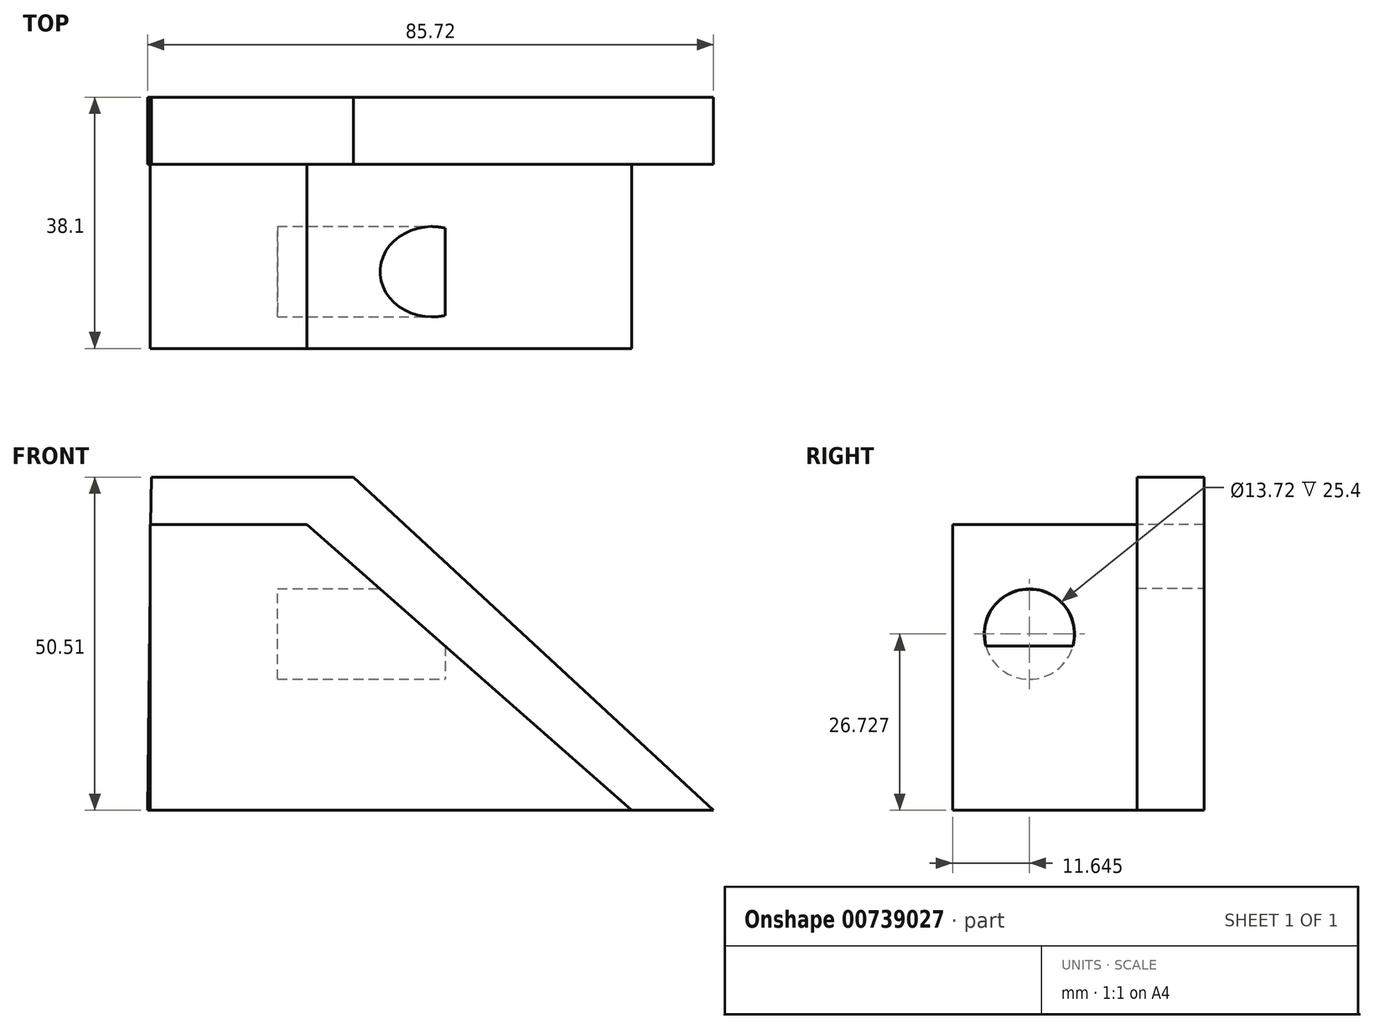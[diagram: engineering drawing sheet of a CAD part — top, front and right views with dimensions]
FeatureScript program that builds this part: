
annotation { "Feature Type Name" : "Feature", "Feature Type Description" : "" }
export const myFeature = defineFeature(function(context is Context, id is Id, definition is map)
    precondition{}
    {
        {
            var Q0;
            Q0=qCreatedBy(makeId("Front.planeOp"),FACE);
            var sketch = newSketch(context, id + "F0", { "sketchPlane" : qUnion([Q0])});
            skLineSegment(sketch, "E0", {"start": v(-44.52, 33.83) * mm, "end": v(-13.92, 33.83) * mm});
            skLineSegment(sketch, "E1", {"start": v(-13.92, 33.83) * mm, "end": v(40.65, -16.68) * mm});
            skLineSegment(sketch, "E2", {"start": v(40.65, -16.68) * mm, "end": v(-45.07, -16.68) * mm});
            skLineSegment(sketch, "E3", {"start": v(-45.07, -16.68) * mm, "end": v(-44.52, 33.83) * mm});
            skSolve(sketch);
        }
        {
            var Q0;
            Q0 = qSketchRegion(id + "F0", true);
            extrude(context, id + "F1", {"entities" : qUnion([Q0]), "depth" : 10.16 * mm, "offsetDistance" : 25.4 * mm});
        }
        {
            var Q0;
            Q0=qCreatedBy(makeId("Front.planeOp"),FACE);
            var sketch = newSketch(context, id + "F2", { "sketchPlane" : qUnion([Q0])});
            skLineSegment(sketch, "E4", {"start": v(-44.7, 28.85) * mm, "end": v(-44.7, -16.68) * mm});
            skLineSegment(sketch, "E5", {"start": v(-44.7, -16.68) * mm, "end": v(28.3, -16.68) * mm});
            skLineSegment(sketch, "E6", {"start": v(28.3, -16.68) * mm, "end": v(-20.92, 26.64) * mm});
            skLineSegment(sketch, "E7", {"start": v(-20.92, 26.64) * mm, "end": v(-44.7, 26.64) * mm});
            skLineSegment(sketch, "E8", {"start": v(-44.7, 26.64) * mm, "end": v(-44.7, 28.85) * mm});
            skSolve(sketch);
        }
        {
            var Q0;
            Q0 = qSketchRegion(id + "F2", true);
            extrude(context, id + "F3", {"entities" : qUnion([Q0]), "operationType" : NewBodyOperationType.ADD, "depth" : 38.1 * mm, "offsetDistance" : 25.4 * mm});
        }
        {
            var Q0;
            Q0=qCreatedBy(makeId("Right.planeOp"),FACE);
            var sketch = newSketch(context, id + "F4", { "sketchPlane" : qUnion([Q0])});
            skCircle(sketch, "E9", {"center": v(-26.45, 10.05) * mm, "radius": 6.86 * mm});
            skSolve(sketch);
        }
        {
            var Q0;
            Q0 = qSketchRegion(id + "F4", true);
            extrude(context, id + "F5", {"entities" : qUnion([Q0]), "operationType" : NewBodyOperationType.REMOVE, "oppositeDirection" : true, "depth" : 25.4 * mm, "offsetDistance" : 25.4 * mm});
        }
    });
